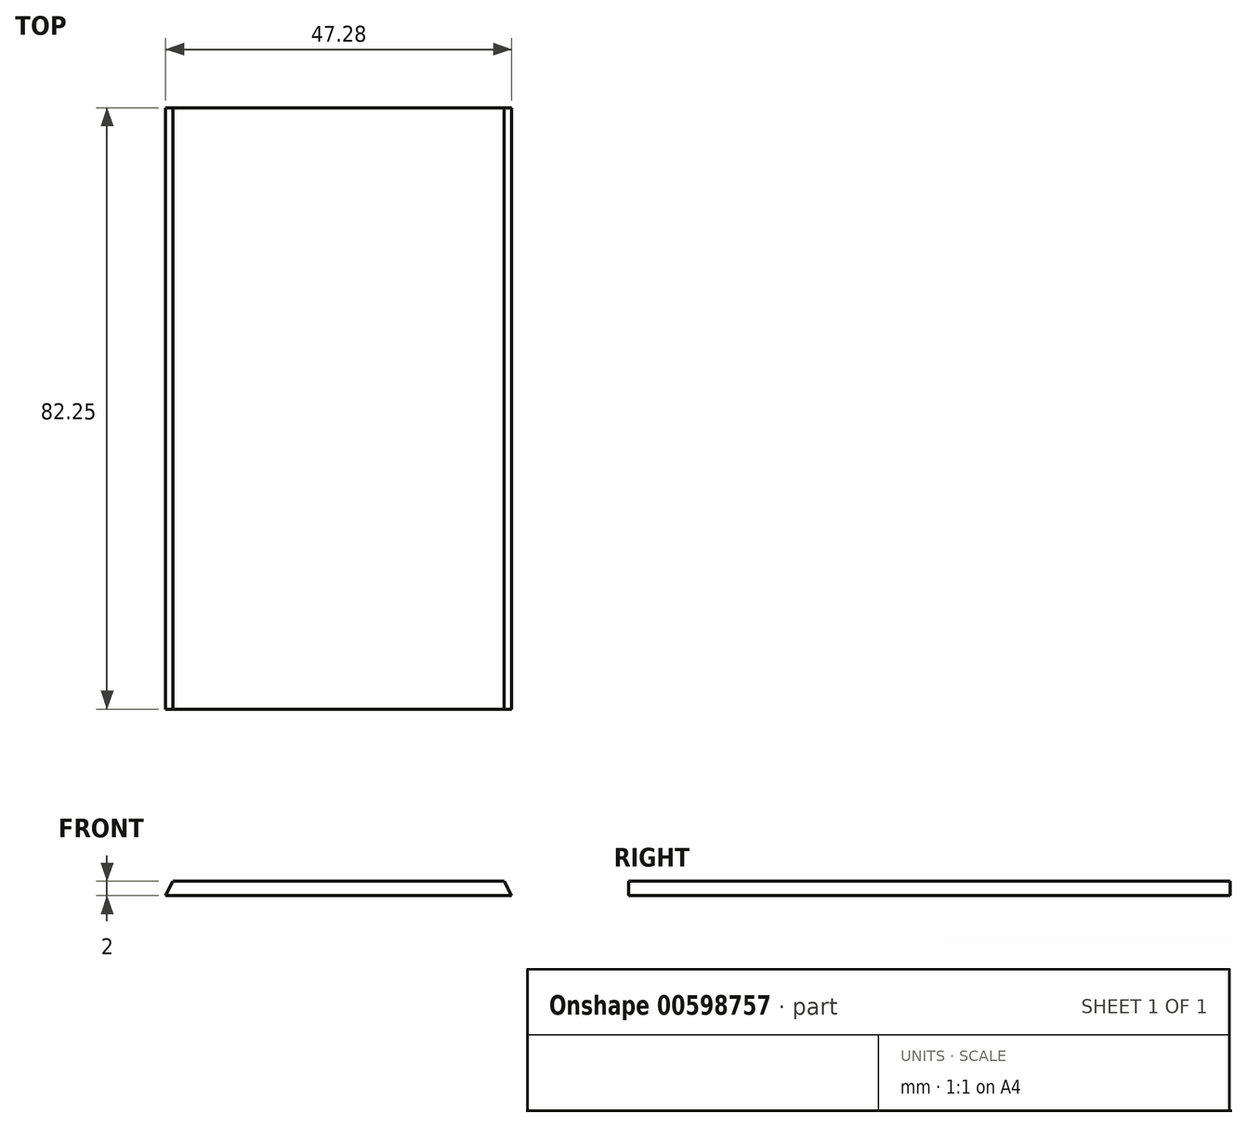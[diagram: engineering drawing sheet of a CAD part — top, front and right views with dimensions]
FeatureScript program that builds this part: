
annotation { "Feature Type Name" : "Feature", "Feature Type Description" : "" }
export const myFeature = defineFeature(function(context is Context, id is Id, definition is map)
    precondition{}
    {
        {
            var Q0;
            Q0=qCreatedBy(makeId("Front.planeOp"),FACE);
            var sketch = newSketch(context, id + "F0", { "sketchPlane" : qUnion([Q0])});
            skLineSegment(sketch, "E0.bottom", {"start": v(-24.64, 1) * mm, "end": v(24.64, 1) * mm});
            skLineSegment(sketch, "E0.top", {"start": v(-24.64, -1) * mm, "end": v(24.64, -1) * mm});
            skLineSegment(sketch, "E0.left", {"start": v(-24.64, 1) * mm, "end": v(-24.64, -1) * mm});
            skLineSegment(sketch, "E0.right", {"start": v(24.64, 1) * mm, "end": v(24.64, -1) * mm});
            skPoint(sketch, "E0.middle", {"position": v(0, 0) * mm});
            skSolve(sketch);
        }
        {
            var Q0;
            Q0=makeQuery(id+"F0.imprint","IMPRINT",FACE,{"disambiguationData":[TD([[makeQuery(id+"F0.imprint","IMPRINT",EDGE,{"derivedFrom":sQuery(id+"F0.wireOp",EDGE,"E0.bottom")}),-1.0]])]});
            extrude(context, id + "F1", {"entities" : qUnion([Q0]), "depth" : 82.25 * mm, "offsetDistance" : 25 * mm});
        }
        {
            var Q0;
            Q0=makeQuery(id+"F1.opExtrude","CAP_FACE",FACE,{"disambiguationData":[OSD([sQuery(id+"F0.wireOp",EDGE,"E0.bottom"),sQuery(id+"F0.wireOp",EDGE,"E0.top"),sQuery(id+"F0.wireOp",EDGE,"E0.left"),sQuery(id+"F0.wireOp",EDGE,"E0.right")])],"isStart":false});
            var sketch = newSketch(context, id + "F2", { "sketchPlane" : qUnion([Q0])});
            skLineSegment(sketch, "E1", {"start": v(-24.64, -1) * mm, "end": v(-23.64, -1) * mm});
            skLineSegment(sketch, "E2", {"start": v(24.64, -1) * mm, "end": v(23.64, -1) * mm});
            skLineSegment(sketch, "E3", {"start": v(24.64, 1) * mm, "end": v(22.64, 1) * mm});
            skLineSegment(sketch, "E4", {"start": v(-24.64, 1) * mm, "end": v(-22.64, 1) * mm});
            skLineSegment(sketch, "E5", {"start": v(-22.64, 1) * mm, "end": v(-23.64, -1) * mm});
            skLineSegment(sketch, "E6", {"start": v(22.64, 1) * mm, "end": v(23.64, -1) * mm});
            skSolve(sketch);
        }
        {
            var Q0;
            Q0=makeQuery(id+"F2.imprint","IMPRINT",FACE,{"disambiguationData":[TD([[makeQuery(id+"F2.imprint","IMPRINT",EDGE,{"derivedFrom":sQuery(id+"F2.wireOp",EDGE,"E1")}),1.0]])]});
            var Q1;
            Q1=makeQuery(id+"F2.imprint","IMPRINT",FACE,{"disambiguationData":[TD([[makeQuery(id+"F2.imprint","IMPRINT",EDGE,{"derivedFrom":sQuery(id+"F2.wireOp",EDGE,"E2")}),1.0]])]});
            extrude(context, id + "F3", {"entities" : qUnion([Q0, Q1]), "operationType" : NewBodyOperationType.REMOVE, "oppositeDirection" : true, "depth" : 82.25 * mm, "offsetDistance" : 25 * mm});
        }
    });
